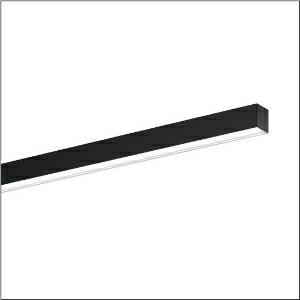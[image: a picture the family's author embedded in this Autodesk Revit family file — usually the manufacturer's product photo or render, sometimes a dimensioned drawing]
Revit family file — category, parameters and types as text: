
# Revit family: silica_r__21_51mx23tbt5b_7df7
name_source: partatom
category: Lighting Fixtures
units: mm (PartAtom-declared; Revit-internal decimal feet)

## family parameters
Cut with Voids When Loaded = No
Host = Face
Light Source = No
Part Type = Normal
Room Calculation Point = No
Round Connector Dimension = Use Diameter
Shared = No

## types (1)
- --- (1 x LED, 4030 lm, 40.5 W, 6500K)
    Apparent Load = 41 VA
    CIE Flux Codes = 78 96 99 100 100
    Color Rendering = 80
    Color Temperature = 6500K
    Default Elevation = 1800 mm
    Description = Silica® 21, office luminaire, primary optical cover: prismatic diffuser, of PMMA, CAT 2 (L<= 3000cd/m²), light emission: direct distribution, primary light characteristic: symmetric, installation type: surface-mounted, LED, rated luminous flux: 4.030lm, luminous efficacy: 95lm/W, light colour: 8tw, colour temperature: 2700..6500K, control gear: DALI DT8, with terminal, 3+2-pole, max. 2.5mm², mains connection: 220..240V, AC, 50/60Hz, rated input power: 42.6W, luminaire housing, of aluminium, matt jet black (RAL 9005), length: 1.504mm, width: 53mm, height: 53mm, protection rating (complete): IP20, insulation class (complete): insulation class I (protective earthing), certification: CE, permissible operating ambient temperature: 0..+35°C, standard: EN 50419, packaging unit: 1 piece
    Height = 53 mm
    Lamp = 1 x LED
    Lamp Light Flux = 4030 lm
    Lamp Power = 40.5 W
    Lamp count = 1
    Length = 1504 mm
    Luminous efficacy = 100 lm/W
    Manufacturer = Siteco
    ModVariant = No
    Model = 51MX23TBT5B
    Mounting Place = Ceiling
    Mounting Type = Surface mounted
    Number of Poles = 1
    OnlyDefault = Yes
    Power Factor = 1
    Product Name = Silica® 21
    Product group = office luminaire | ceiling mounted
    ProductGroupID = 302
    Protection Class = Protection class I
    Protection Degree = IP 20
    RLX_Detail_Level = 1
    RLX_Emergency_Light_Flux = 0 lm
    RLX_Emergency_Type = 0
    RLX_Emergency_Type_DB = No
    RlxData = <blob elided: 20437 chars, md5=e3bdda38>
    Socket = socket
    Standby Power = 0 W
    System Light Flux = 4030 lm
    System Power = 41 W
    Type Comments = individual setting
    Type Image = l_1335925.jpg
    URL = http://relux.com
    VarID = @adj_139812
    Voltage = 0 V
    Weight = 0.00 kg
    Width = 53 mm

## geometry (parser evidence)
native form markers: Blend x4, Sweep x10
no freeform markers — native parametric forms only
